# Revit family: BIM_Model_Sanimat_1002_50_D
name_source: partatom
category: Mechanical Equipment
revit_build: Autodesk Revit 2018 (Build: 20170223_1515(x64)
units: mm (PartAtom-declared; Revit-internal decimal feet)

## family parameters
Always vertical = Yes
Cut with Voids When Loaded = No
Part Type = Normal
Room Calculation Point = No
Round Connector Dimension = Use Radius
Shared = No
Work Plane-Based = No

## types (1)
- Sanimat 1002 D
    Cable Length (m) = 4 + 1.5
    Capacity (m3/hr) = 40 m³
    Description = Flood-proof double lifting station for automatic sewage pumping from areas below the backwash level in accordance with EN 12050-1. It is ideal for effective sewage removal from apartments, large buildings, and for both new and renovated structures.
    Discharge Connection = Sleeve 4'' DN 100
    Discharge Flange DN 80 = 40 mm  [stored 0.131234 ft]
    Head (m) = 11 mm  [stored 0.0360892 ft]
    Impeller = Cast Iron EN-GJL-250
    Inflow / Vent DN 100 = 50 mm  [stored 0.164042 ft]
    Inflow / Vent DN 70 = 35 mm  [stored 0.114829 ft]
    Inflow DN 100 = 50 mm  [stored 0.164042 ft]
    Inflow DN 150 = 75 mm
    Inflow DN 50 = 25 mm  [stored 0.082021 ft]
    Inflow/Hand Membrane Pump DN 40 = 20 mm  [stored 0.0656168 ft]
    Manufacturer = Sulzer
    Model = Lifting Station Type ABS Sanimat 1002
    Motor Housing = Cast Iron EN-GJL-250
    Motor Power (kW) = P1=1.77 P2=1.40
    Product Specification Link = http://www.sulzer.com
    Rated Current (A) = 3.5
    Rated Voltage (V) = 400 3~
    Rotor Shaft = Stainless steel 1.4021 (AISI 420)
    Speed (r/min) = 1450
    Tank Material = Polyethylene
    Volute = Polyethylene
    Weight (Kg) = 115

note: [stored X ft] marks values corroborated as IEEE doubles in the binary element streams (Revit-internal decimal feet)

## geometry (parser evidence)
native form markers: Sweep x2
no freeform markers — native parametric forms only
